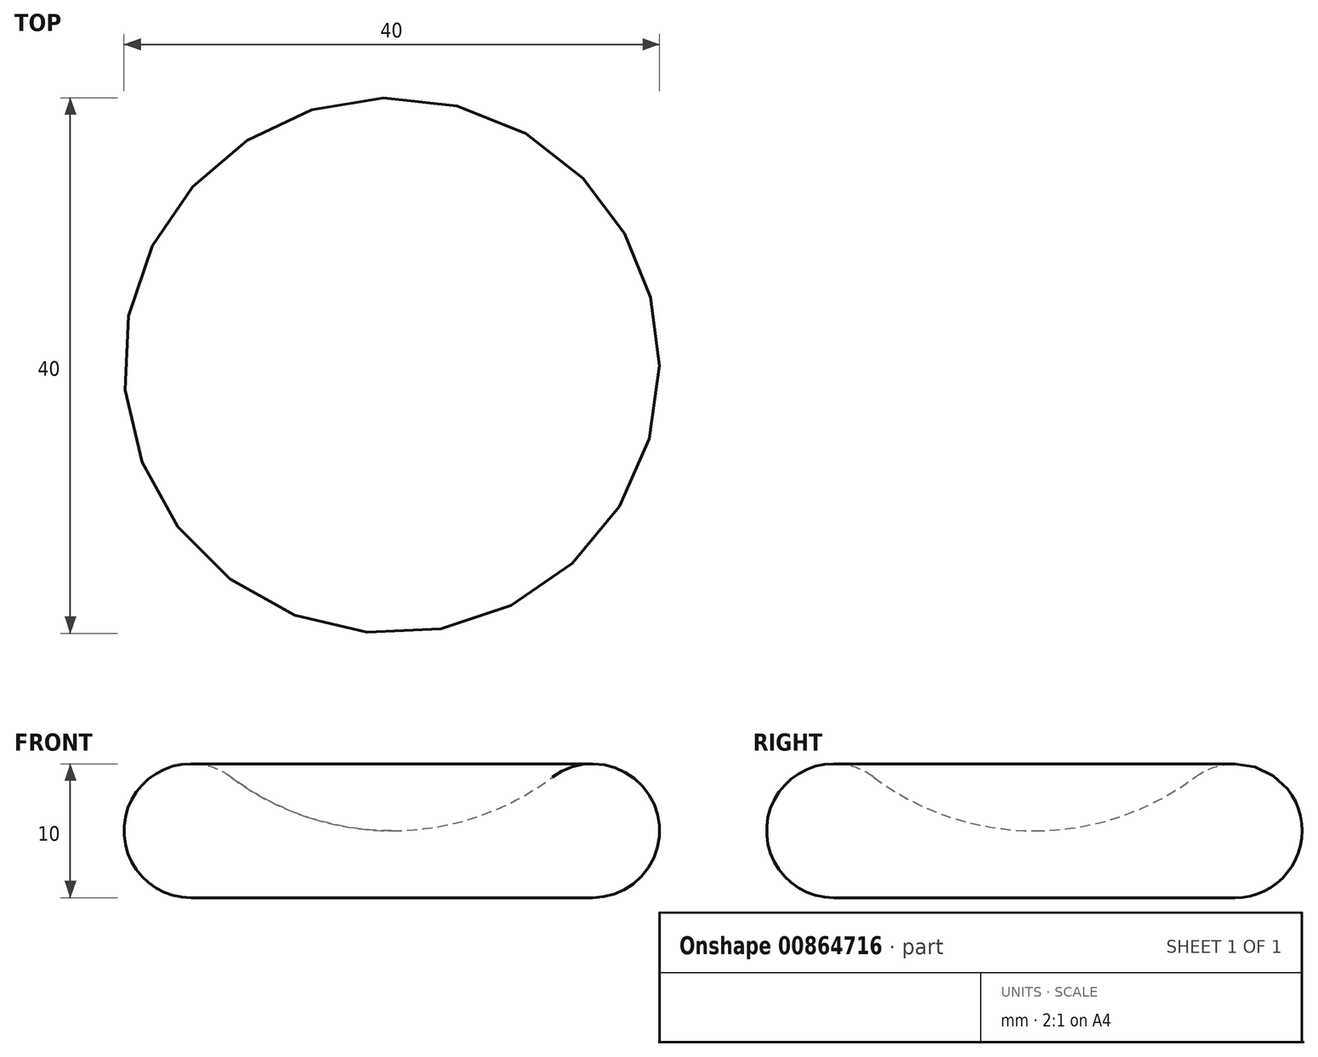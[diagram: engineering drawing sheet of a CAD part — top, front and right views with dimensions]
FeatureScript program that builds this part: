
annotation { "Feature Type Name" : "Feature", "Feature Type Description" : "" }
export const myFeature = defineFeature(function(context is Context, id is Id, definition is map)
    precondition{}
    {
        {
            var Q0;
            Q0=qCreatedBy(makeId("Front.planeOp"),FACE);
            var sketch = newSketch(context, id + "F0", { "sketchPlane" : qUnion([Q0])});
            skArc(sketch, "E0", {"start": v(-12, 9) * mm, "mid": v(-19.74, 6.58) * mm, "end": v(-15, 0) * mm});
            skArc(sketch, "E1", {"start": v(-12, 9) * mm, "mid": v(-6.32, 6.03) * mm, "end": v(0, 5) * mm});
            skLineSegment(sketch, "E2", {"start": v(-15, 0) * mm, "end": v(0, 0) * mm});
            skLineSegment(sketch, "E3", {"start": v(0, 5) * mm, "end": v(0, 0) * mm});
            skSolve(sketch);
        }
        {
            var Q0;
            Q0=makeQuery(id+"F0.imprint","IMPRINT",FACE,{"disambiguationData":[TD([[makeQuery(id+"F0.imprint","IMPRINT",EDGE,{"derivedFrom":sQuery(id+"F0.wireOp",EDGE,"E0")}),1.0]])]});
            var Q1;
            Q1=sQuery(id+"F0.wireOp",EDGE,"E3");
            revolve(context, id + "F1", {"surfaceOperationType" : NewSurfaceOperationType.NEW, "entities" : qUnion([Q0]), "axis" : qUnion([Q1]), "revolveType" : RevolveType.FULL});
        }
    });
